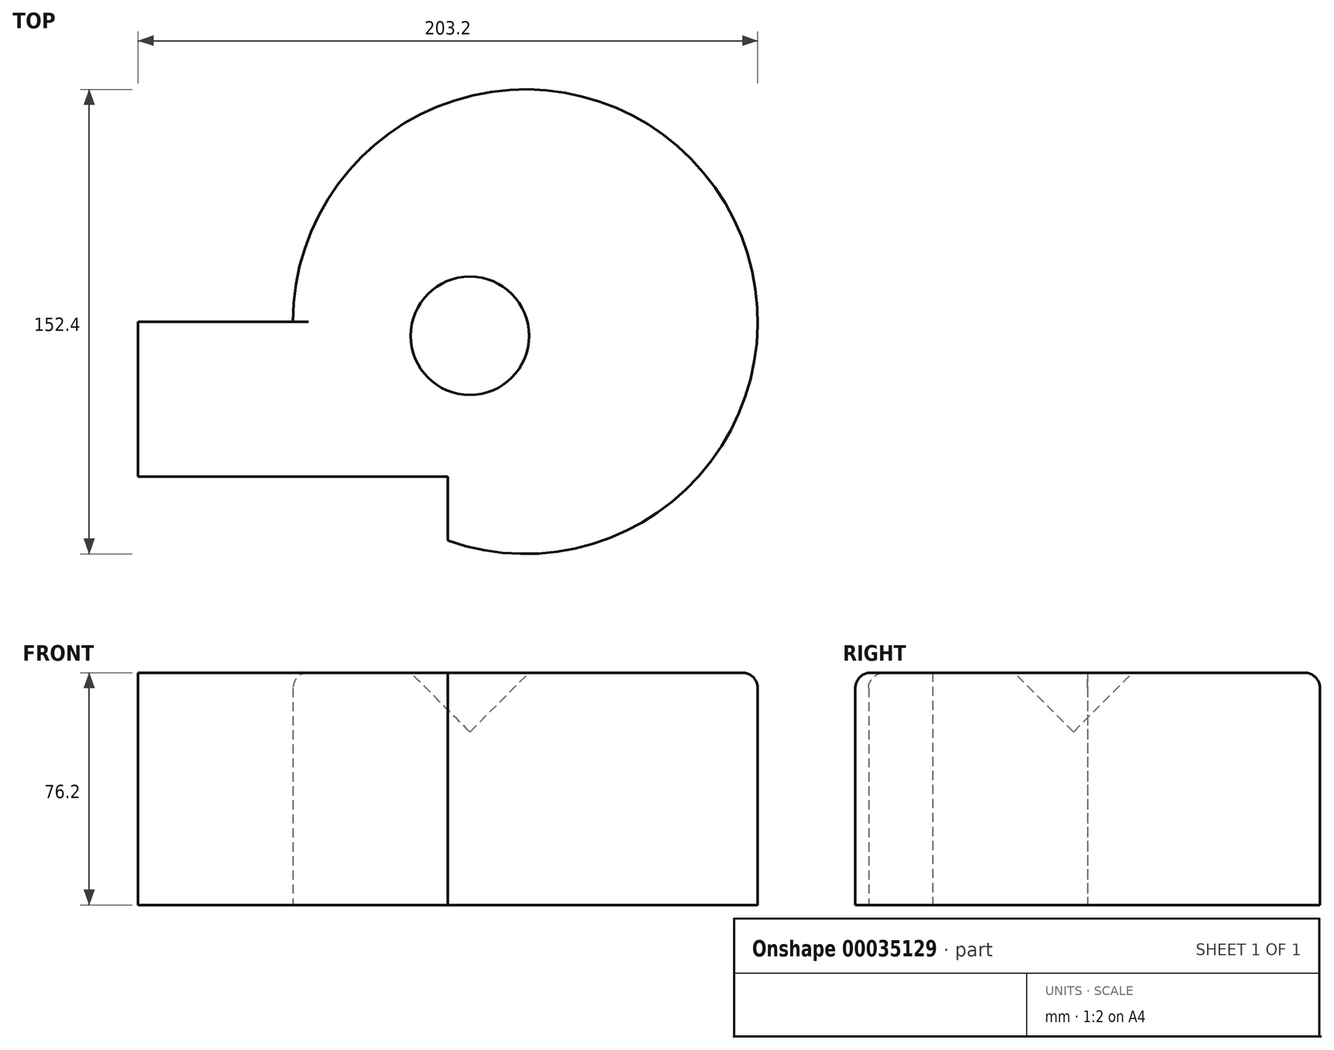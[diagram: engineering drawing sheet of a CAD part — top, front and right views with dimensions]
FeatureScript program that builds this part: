
annotation { "Feature Type Name" : "Feature", "Feature Type Description" : "" }
export const myFeature = defineFeature(function(context is Context, id is Id, definition is map)
    precondition{}
    {
        {
            var Q0;
            Q0=qCreatedBy(makeId("Top.planeOp"),FACE);
            var sketch = newSketch(context, id + "F0", { "sketchPlane" : qUnion([Q0])});
            skLineSegment(sketch, "E0.bottom", {"start": v(0, 0) * mm, "end": v(101.6, 0) * mm});
            skLineSegment(sketch, "E0.top", {"start": v(0, 50.8) * mm, "end": v(50.8, 50.8) * mm});
            skLineSegment(sketch, "E0.left", {"start": v(0, 0) * mm, "end": v(0, 50.8) * mm});
            skLineSegment(sketch, "E0.right", {"start": v(101.6, -21.04) * mm, "end": v(101.6, 0) * mm});
            skArc(sketch, "E1", {"start": v(101.6, -21.04) * mm, "mid": v(189.22, 94.8) * mm, "end": v(50.8, 50.8) * mm});
            skSolve(sketch);
        }
        {
            var Q0;
            Q0=makeQuery(id+"F0.imprint","IMPRINT",FACE,{"disambiguationData":[TD([[makeQuery(id+"F0.imprint","IMPRINT",EDGE,{"derivedFrom":sQuery(id+"F0.wireOp",EDGE,"E0.bottom")}),1.0]])]});
            extrude(context, id + "F1", {"entities" : qUnion([Q0]), "depth" : 76.2 * mm});
        }
        {
            var Q0;
            Q0=makeQuery(id+"F1.opExtrude","CAP_EDGE",EDGE,{"disambiguationData":[OSD([sQuery(id+"F0.wireOp",EDGE,"E1")])],"isStart":false});
            fillet(context, id + "F2", {"entities" : qUnion([Q0]), "radius" : 5.08 * mm, "tangentPropagation" : true, "allowEdgeOverflow" : false});
        }
        {
            var Q0;
            Q0=makeQuery(id+"F1.opExtrude","CAP_FACE",FACE,{"disambiguationData":[OSD([sQuery(id+"F0.wireOp",EDGE,"E0.bottom"),sQuery(id+"F0.wireOp",EDGE,"E0.top"),sQuery(id+"F0.wireOp",EDGE,"E0.left"),sQuery(id+"F0.wireOp",EDGE,"E0.right"),sQuery(id+"F0.wireOp",EDGE,"E1")])],"isStart":false});
            var sketch = newSketch(context, id + "F3", { "sketchPlane" : qUnion([Q0])});
            skCircle(sketch, "E2", {"center": v(108.8, 46.14) * mm, "radius": 19.42 * mm});
            skSolve(sketch);
        }
        {
            var Q0;
            Q0=makeQuery(id+"F3.imprint","IMPRINT",FACE,{"disambiguationData":[TD([[makeQuery(id+"F3.imprint","IMPRINT",EDGE,{"derivedFrom":sQuery(id+"F3.wireOp",EDGE,"E2")}),1.0]])]});
            extrude(context, id + "F4", {"entities" : qUnion([Q0]), "operationType" : NewBodyOperationType.REMOVE, "oppositeDirection" : true, "depth" : 25.4 * mm, "hasDraft" : true, "draftAngle" : 45 * degree, "draftPullDirection" : true});
        }
    });
